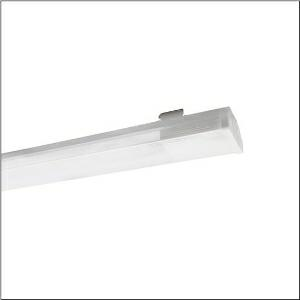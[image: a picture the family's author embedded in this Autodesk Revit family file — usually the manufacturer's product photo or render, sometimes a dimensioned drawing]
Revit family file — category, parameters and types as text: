
# Revit family: modario_r__31_gen_2_53bm813du4f5c2_7251
name_source: partatom
category: Lighting Fixtures
units: mm (PartAtom-declared; Revit-internal decimal feet)

## family parameters
Cut with Voids When Loaded = No
Host = Face
Light Source = No
Part Type = Normal
Room Calculation Point = No
Round Connector Dimension = Use Diameter
Shared = No

## types (1)
- --- (1 x LED, 15920 lm, 92.1 W, 4000K)
    Apparent Load = 92 VA
    CIE Flux Codes = 62 83 95 93 100
    Color Rendering = 80
    Color Temperature = 4000K
    Default Elevation = 1800 mm
    Description = Modario® 31 Gen.2, luminaire insert, of sheet steel, coil coated, white, length: 2.392mm, width: 81mm, height: 82mm, 8x system unit, system units: 299mm, LED rated luminous flux: 15.920lm, light colour: 840, control gear: DALI 2, control gear: ECG DALI, with plug, 5-pole, with phase selection, mains connection: 220..240V, AC, 50/60Hz, rated input power: 92W, through-wiring accessed according to module size, primary optical cover: cover, of PMMA, light emission: direct distribution, primary light characteristic: symmetric, protection rating (complete): IP20, protection rating (LED compartment): IP50, insulation class (complete): insulation class I (protective earthing), certification: CE, ENEC, VDE, UKCA, impact resistance: IK03, permissible ambient temperature for indoor applications: -25..+40°C, corresponds to IFS (International Featured Standards) requirements for safety and quality in the food industry, reducing of maximum allowable ambient temperature of 5°C with ceiling mounting, packaging unit: 1 piece
    Height = 92 mm
    Lamp = 1 x LED
    Lamp Light Flux = 15920 lm
    Lamp Power = 92.1 W
    Lamp count = 1
    Length = 2392 mm
    Luminous efficacy = 173 lm/W
    Manufacturer = Siteco
    ModVariant = No
    Model = 53BM813DU4F5C2
    Mounting Place = Ceiling
    Mounting Type = Pendant
    Number of Poles = 1
    OnlyDefault = Yes
    Power Factor = 1
    Product Name = Modario® 31 Gen.2
    Product group = luminaire insert | ceiling pendant
    ProductGroupID = 902
    Protection Class = Protection class I
    Protection Degree = IP 20
    RLX_Detail_Level = 1
    RLX_Emergency_Light_Flux = 0 lm
    RLX_Emergency_Type = 0
    RLX_Emergency_Type_DB = No
    RlxData = <blob elided: 38473 chars, md5=be36d2af>
    Socket = socket
    Standby Power = 0 W
    System Light Flux = 15920 lm
    System Power = 92 W
    Type Comments = factory setting: luminous flux: 100 % | dim-lin: 254 | 418 mA
    Type Image = l_1341883.jpg
    URL = http://relux.com
    VarID = @adj_064923
    Voltage = 0 V
    Weight = 0.00 kg
    Width = 81 mm

## geometry (parser evidence)
native form markers: Blend x4, Sweep x13
no freeform markers — native parametric forms only
